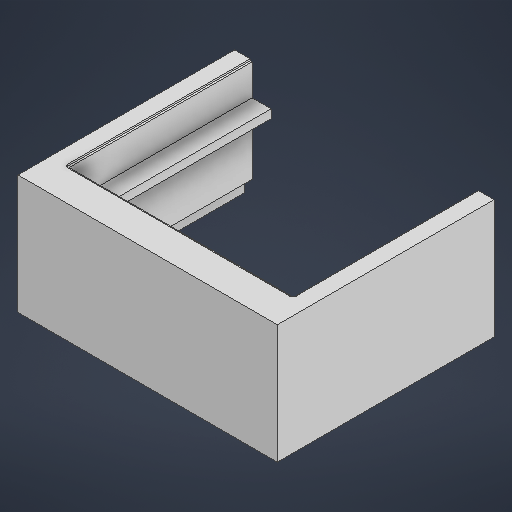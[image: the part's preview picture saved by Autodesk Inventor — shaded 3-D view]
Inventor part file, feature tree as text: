
AUTODESK INVENTOR PART (.ipt)
format: ipt  version: 2025.2 (Build 292293000, 293)  size: 374,784 bytes
history: native  units: in
note: dims shown in document units (in); Inventor stores cm internally (conversion verified against a paired STEP export)
features: sketch x13, extrude x12, split x1
ambient origin geometry x8: Origin, YZ Plane, XZ Plane, XY Plane, X Axis, Y Axis, Z Axis, Center Point
bodies: Solid1 (feature_tree)
feature tree (26):
  extrude  "Extrusion1"  Depth=6.5748in
  extrude  "Extrusion2"  Depth=5.7874in
  extrude  "Extrusion3"  Depth=0.0787in
  extrude  "Extrusion4"  Depth=0.0492in
  extrude  "Extrusion5"  Depth=5.689in
  extrude  "Extrusion8"  Depth=0.7874in TaperAngle=0.0deg
  extrude  "Extrusion9"  Depth=0.2362in
  extrude  "Extrusion10"  Depth=0.1575in
  extrude  "Extrusion11"  Depth=0.2264in
  extrude  "Extrusion12"  Depth=0.2264in
  split  "Split1"
  extrude  "Extrusion15"  Depth=0.1575in
  extrude  "Extrusion16"  Depth=0.2264in
  sketch  "Sketch1"  dims[d0=6.5748in d1=10.9843in]
  sketch  "Sketch2"  dims[d2=1.0472in d3=0.0in d4=5.7874in]
  sketch  "Sketch3"  dims[d5=9.4094in d6=0.0787in]
  sketch  "Sketch4"  dims[d7=0.0433in d8=0.0in d9=0.0492in]
  sketch  "Sketch5"  dims[d10=0.0657in d11=5.689in]
  sketch  "Sketch8"  dims[d12=9.0591in d13=0.7874in d14=0.0in]
  sketch  "Sketch9"  dims[d15=0.1575in d16=0.2362in]
  sketch  "Sketch10"  dims[d17=0.2264in d18=0.1575in]
  sketch  "Sketch12"  dims[d19=0.2362in d20=0.2264in]
  sketch  "Sketch13"  dims[d21=0.1575in d22=0.2264in]
  sketch  "Sketch14"  dims[d23=0.2362in d24=0.1575in]
  sketch  "Sketch18"  dims[d25=0.2362in d26=0.2264in]
  sketch  "Sketch19"  dims[d27=0.4055in d28=0.0in d29=0.0984in d30=0.0984in d31=0.0984in d32=0.0984in d33=0.4055in d34=0.0in d35=0.2165in d36=0.0in d49=0.1378in d50=0.1378in d51=0.1378in d52=0.1378in d53=0.5433in d54=0.0in d55=4.7244in d56=7.874in d57=0.2283in d58=0.0in d59=1.5748in d60=0.0in d67=5.689in d68=9.0591in d69=0.1969in d70=0.1969in d71=9.4528in d72=0.1969in d73=0.1969in d74=9.4528in d75=0.3937in d76=0.0in d77=0.0984in d78=0.2362in d79=0.2362in d80=0.0984in d81=0.2362in d82=0.2362in d83=0.0984in d84=0.2362in d85=0.2362in d86=0.2362in d87=0.2362in d88=0.3937in d89=0.0in d94=6.6186in d95=0.0in d97=0.1969in d99=0.1969in d101=0.1969in d102=0.1969in d104=0.1969in d106=0.1969in d107=0.5906in d108=0.0in d47=0.0197in d48=0.0344in]
